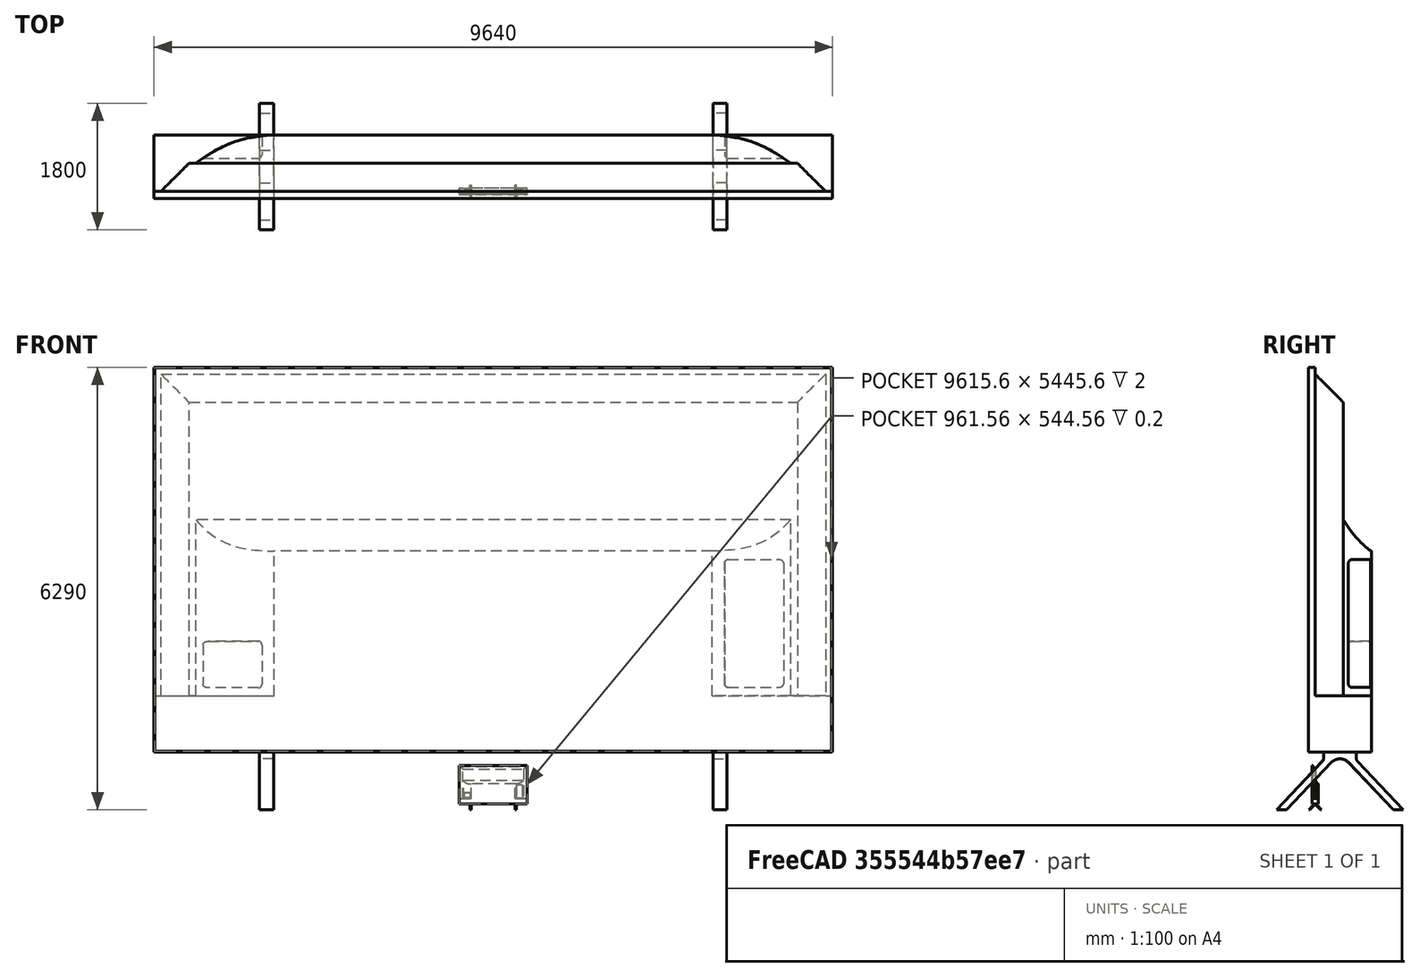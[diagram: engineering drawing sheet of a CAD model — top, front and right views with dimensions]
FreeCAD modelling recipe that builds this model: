
FCSTD DOCUMENT  (FreeCAD 1.0R39109 (Git))
Label: tv
License: All rights reserved
LicenseURL: https://en.wikipedia.org/wiki/All_rights_reserved
objects: Sketcher::SketchObject×9, PartDesign::Pad×6, PartDesign::Pocket×3, PartDesign::Body×3, App::Link×3, PartDesign::Fillet×2, Assembly::JointGroup×2, Assembly::AssemblyObject×2, Part::FeaturePython×2, PartDesign::ShapeBinder×2, PartDesign::Plane×2, App::Part×1
note: 60 computed .brp shape members not serialized (recipe doc carries the construction recipe); baked Part::Feature solids carry a one-line shape summary decoded from their .brp

FEATURE [Sketcher::SketchObject] Sketch003
  ArcFitTolerance = 1e-06
  AttachmentSupport = -> [XZ_Plane]
  FullyConstrained = true
  MakeInternals = false
  MapMode = 5
  Placement = pos=(0,0,0) rot=(1,0,0;1.5708rad)
  sketch-geometry (5):
    g0: LineSegment StartX=-4820 StartY=820 StartZ=0 EndX=4820 EndY=820 EndZ=0
    g1: LineSegment StartX=4820 StartY=820 StartZ=0 EndX=4820 EndY=6290 EndZ=0
    g2: LineSegment StartX=4820 StartY=6290 StartZ=0 EndX=-4820 EndY=6290 EndZ=0
    g3: LineSegment StartX=-4820 StartY=6290 StartZ=0 EndX=-4820 EndY=820 EndZ=0
    g4: GeomPoint [constr] X=0 Y=3555 Z=0
  constraints (13):
    c: Coincident(g0,g1)
    c: Coincident(g1,g2)
    c: Coincident(g2,g3)
    c: Coincident(g3,g0)
    c: Horizontal(g0)
    c: Horizontal(g2)
    c: Vertical(g1)
    c: Vertical(g3)
    c: Symmetric(g2,g0,g4)
    c: Distance(g1,g3) = 9640
    c: PointOnObject(g4,g-2)
    c: DistanceY(g1,g1) = 5470
    c: DistanceY(g0) = 820
FEATURE [PartDesign::Pad] Pad
  Direction = (0,-1,2e-16)
  Length = 100
  Length2 = 10
  Placement = pos=(0,0,0) rot=(1,0,0;1.5708rad)
  Profile = -> Sketch003
  ReferenceAxis = -> Sketch003 [N_Axis]
  Refine = true
  Suppressed = false
  Type = 0
FEATURE [Sketcher::SketchObject] Sketch004
  ArcFitTolerance = 1e-06
  AttachmentSupport = -> [Pad]
  ExternalGeometry = -> [Pad]
  FullyConstrained = true
  MakeInternals = false
  MapMode = 5
  Placement = pos=(0,7.894e-13,0) rot=(-1,0,0;1.5708rad)
  sketch-geometry (4):
    g0: LineSegment StartX=-4820 StartY=-820 StartZ=0 EndX=-4820 EndY=-1620 EndZ=0
    g1: LineSegment StartX=-4820 StartY=-1620 StartZ=0 EndX=4820 EndY=-1620 EndZ=0
    g2: LineSegment StartX=4820 StartY=-1620 StartZ=0 EndX=4820 EndY=-820 EndZ=0
    g3: LineSegment StartX=4820 StartY=-820 StartZ=0 EndX=-4820 EndY=-820 EndZ=0
  constraints (10):
    c: Coincident(g0,g1)
    c: Coincident(g1,g2)
    c: Coincident(g2,g3)
    c: Coincident(g3,g0)
    c: Vertical(g0)
    c: Vertical(g2)
    c: Horizontal(g1)
    c: DistanceY(g0,g0) = 800
    c: Coincident(g2,g-3)
    c: Coincident(g0,g-4)
FEATURE [PartDesign::Pad] Pad001
  BaseFeature = -> Pad
  Direction = (0,1,2e-16)
  Length = 800
  Length2 = 10
  Placement = pos=(0,0,0) rot=(1,0,0;1.5708rad)
  Profile = -> Sketch004
  ReferenceAxis = -> Sketch004 [N_Axis]
  Refine = true
  Suppressed = false
  Type = 0
FEATURE [Sketcher::SketchObject] Sketch005
  ArcFitTolerance = 1e-06
  AttachmentSupport = -> [Pad001]
  ExternalGeometry = -> [Pad001]
  FullyConstrained = false
  MakeInternals = false
  MapMode = 5
  Placement = pos=(0,7.894e-13,0) rot=(-1,0,0;1.5708rad)
  sketch-geometry (4):
    g0: LineSegment StartX=-4720 StartY=-6190 StartZ=0 EndX=4720 EndY=-6190 EndZ=0
    g1: LineSegment StartX=4720 StartY=-6190 StartZ=0 EndX=4720 EndY=-963.315 EndZ=0
    g2: LineSegment StartX=4720 StartY=-963.315 StartZ=0 EndX=-4720 EndY=-963.315 EndZ=0
    g3: LineSegment StartX=-4720 StartY=-963.315 StartZ=0 EndX=-4720 EndY=-6190 EndZ=0
  constraints (11):
    c: Coincident(g0,g1)
    c: Coincident(g1,g2)
    c: Coincident(g2,g3)
    c: Coincident(g3,g0)
    c: Horizontal(g0)
    c: Horizontal(g2)
    c: Vertical(g1)
    c: Vertical(g3)
    c: DistanceY(g-3,g0) = 100
    c: DistanceX(g-3,g0) = 100
    c: DistanceX(g0,g-4) = 100
FEATURE [PartDesign::Pad] Pad002
  BaseFeature = -> Pad001
  Direction = (0,1,2e-16)
  Length = 400
  Length2 = 10
  Placement = pos=(0,0,0) rot=(1,0,0;1.5708rad)
  Profile = -> Sketch005
  ReferenceAxis = -> Sketch005 [N_Axis]
  Refine = true
  Suppressed = false
  TaperAngle = -45
  Type = 0
FEATURE [Sketcher::SketchObject] Sketch008
  ArcFitTolerance = 1e-06
  AttachmentSupport = -> [Pad002]
  ExternalGeometry = -> [Pad002]
  FullyConstrained = false
  MakeInternals = false
  MapMode = 5
  Placement = pos=(0,0,1620) rot=(0,0,1;3.14159rad)
  sketch-geometry (18):
    g0: LineSegment StartX=0 StartY=-400 StartZ=0 EndX=-4226.42 EndY=-400 EndZ=0
    g1: Circle [constr] CenterX=-4226.42 CenterY=-400 CenterZ=0 NormalX=0 NormalY=0 NormalZ=1 AngleXU=0 Radius=1
    g2: Circle [constr] CenterX=-3745.48 CenterY=-741.541 CenterZ=0 NormalX=0 NormalY=0 NormalZ=1 AngleXU=0 Radius=1
    g3: Circle [constr] CenterX=-3483.42 CenterY=-773.588 CenterZ=0 NormalX=0 NormalY=0 NormalZ=1 AngleXU=0 Radius=1
    g4: BSplineCurve PolesCount=4 KnotsCount=2 Degree=3 IsPeriodic=0
    g5: GeomPoint [constr] X=-4226.42 Y=-400 Z=0
    g6: GeomPoint [constr] X=-3109.89 Y=-800 Z=0
    g7: Circle [constr] CenterX=-3109.89 CenterY=-800 CenterZ=0 NormalX=0 NormalY=0 NormalZ=1 AngleXU=0 Radius=1
    g8: LineSegment StartX=-3109.89 StartY=-800 StartZ=0 EndX=0 EndY=-800 EndZ=0
    g9: Circle [constr] CenterX=4226.42 CenterY=-400 CenterZ=0 NormalX=0 NormalY=0 NormalZ=1 AngleXU=0 Radius=1
    g10: Circle [constr] CenterX=3745.48 CenterY=-741.541 CenterZ=0 NormalX=0 NormalY=0 NormalZ=1 AngleXU=0 Radius=1
    g11: Circle [constr] CenterX=3483.42 CenterY=-773.588 CenterZ=0 NormalX=0 NormalY=0 NormalZ=1 AngleXU=0 Radius=1
    g12: BSplineCurve PolesCount=4 KnotsCount=2 Degree=3 IsPeriodic=0
    g13: GeomPoint [constr] X=4226.42 Y=-400 Z=0
    g14: GeomPoint [constr] X=3109.89 Y=-800 Z=0
    g15: Circle [constr] CenterX=3109.89 CenterY=-800 CenterZ=0 NormalX=0 NormalY=0 NormalZ=1 AngleXU=0 Radius=1
    g16: LineSegment StartX=3109.89 StartY=-800 StartZ=0 EndX=0 EndY=-800 EndZ=0
    g17: LineSegment StartX=0 StartY=-400 StartZ=0 EndX=4226.42 EndY=-400 EndZ=0
  constraints (25):
    c: Horizontal(g0)
    c: PointOnObject(g0,g-3)
    c: Weight(g1) = 1
    c: Equal(g1,g2)
    c: Equal(g1,g3)
    c: InternalAlignment(g1,g4)
    c: InternalAlignment(g2,g4)
    c: InternalAlignment(g3,g4)
    c: InternalAlignment(g5,g4)
    c: InternalAlignment(g6,g4)
    c: Coincident(g1,g0)
    c: InternalAlignment(g7,g4)
    c: Equal(g7,g1)
    c: Horizontal(g17)
    c: Weight(g9) = 1
    c: Equal(g9,g10)
    c: Equal(g9,g11)
    c: InternalAlignment(g9,g12)
    c: InternalAlignment(g10,g12)
    c: InternalAlignment(g11,g12)
    c: InternalAlignment(g13,g12)
    c: InternalAlignment(g14,g12)
    c: Coincident(g9,g17)
    c: InternalAlignment(g15,g12)
    c: Equal(g15,g9)
FEATURE [PartDesign::Pad] Pad003
  BaseFeature = -> Pad002
  Direction = (0,0,1)
  Length = 2500
  Length2 = 10
  Placement = pos=(0,0,0) rot=(1,0,0;1.5708rad)
  Profile = -> Sketch008
  ReferenceAxis = -> Sketch008 [N_Axis]
  Refine = true
  Suppressed = false
  Type = 0
FEATURE [Sketcher::SketchObject] Sketch009
  ArcFitTolerance = 1e-06
  AttachmentSupport = -> [Pad003]
  ExternalGeometry = -> [Pad003]
  FullyConstrained = false
  MakeInternals = false
  MapMode = 5
  Placement = pos=(4820,-4.5308e-12,0) rot=(0.707107,0,0.707107;3.14159rad)
  sketch-geometry (8):
    g0: LineSegment StartX=4120 StartY=-800 StartZ=0 EndX=3674.07 EndY=-800 EndZ=0
    g1: Circle [constr] CenterX=4120 CenterY=-400 CenterZ=0 NormalX=0 NormalY=0 NormalZ=1 AngleXU=0 Radius=1
    g2: Circle [constr] CenterX=3794.85 CenterY=-604.641 CenterZ=0 NormalX=0 NormalY=0 NormalZ=1 AngleXU=0 Radius=1
    g3: Circle [constr] CenterX=3674.07 CenterY=-800 CenterZ=0 NormalX=0 NormalY=0 NormalZ=1 AngleXU=0 Radius=1
    g4: BSplineCurve PolesCount=3 KnotsCount=2 Degree=2 IsPeriodic=0
    g5: GeomPoint [constr] X=4120 Y=-400 Z=0
    g6: GeomPoint [constr] X=3674.07 Y=-800 Z=0
    g7: LineSegment StartX=4120 StartY=-400 StartZ=0 EndX=4120 EndY=-800 EndZ=0
  constraints (12):
    c: Coincident(g0,g-4)
    c: Horizontal(g0)
    c: Weight(g1) = 1
    c: Equal(g1,g2)
    c: Equal(g1,g3)
    c: InternalAlignment(g1,g4)
    c: InternalAlignment(g2,g4)
    c: InternalAlignment(g3,g4)
    c: InternalAlignment(g5,g4)
    c: InternalAlignment(g6,g4)
    c: Coincident(g1,g-4)
    c: Coincident(g3,g0)
FEATURE [PartDesign::Pocket] Pocket
  BaseFeature = -> Pad003
  Direction = (-1,0,2e-16)
  Length = 5
  Length2 = 5
  Placement = pos=(0,0,0) rot=(1,0,0;1.5708rad)
  Profile = -> Sketch009
  ReferenceAxis = -> Sketch009 [N_Axis]
  Refine = true
  Suppressed = false
  Type = 1
FEATURE [Sketcher::SketchObject] Sketch010
  ArcFitTolerance = 1e-06
  AttachmentSupport = -> [Pocket]
  ExternalGeometry = -> [Pocket]
  FullyConstrained = false
  MakeInternals = false
  MapMode = 5
  Placement = pos=(0,800,0) rot=(-1,0,0;1.5708rad)
  sketch-geometry (13):
    g0: LineSegment StartX=4524.01 StartY=-3554.92 StartZ=0 EndX=4524.01 EndY=-1739.15 EndZ=0
    g1: LineSegment StartX=4524.01 StartY=-1739.15 StartZ=0 EndX=3287.44 EndY=-1739.15 EndZ=0
    g2: LineSegment StartX=3287.44 StartY=-1739.15 StartZ=0 EndX=3287.44 EndY=-3554.92 EndZ=0
    g3: LineSegment StartX=3287.44 StartY=-3554.92 StartZ=0 EndX=4524.01 EndY=-3554.92 EndZ=0
    g4: LineSegment StartX=-3287.44 StartY=-2395.51 StartZ=0 EndX=-3287.44 EndY=-1732.57 EndZ=0
    g5: LineSegment StartX=-3287.44 StartY=-1732.57 StartZ=0 EndX=-4524.01 EndY=-1732.57 EndZ=0
    g6: LineSegment StartX=-4524.01 StartY=-1732.57 StartZ=0 EndX=-4524.01 EndY=-2395.51 EndZ=0
    g7: LineSegment StartX=-4524.01 StartY=-2395.51 StartZ=0 EndX=-3287.44 EndY=-2395.51 EndZ=0
    g8: LineSegment [constr] StartX=3287.44 StartY=-3554.92 StartZ=0 EndX=3109.89 EndY=-3554.92 EndZ=0
    g9: LineSegment [constr] StartX=3109.89 StartY=-3554.92 StartZ=0 EndX=3109.89 EndY=-3674.07 EndZ=0
    g10: LineSegment [constr] StartX=3287.44 StartY=-1739.15 StartZ=0 EndX=3109.89 EndY=-1739.15 EndZ=0
    g11: LineSegment [constr] StartX=3109.89 StartY=-1739.15 StartZ=0 EndX=3109.89 EndY=-1620 EndZ=0
    g12: LineSegment [constr] StartX=-3287.44 StartY=-1732.57 StartZ=0 EndX=-3109.89 EndY=-1732.57 EndZ=0
  constraints (32):
    c: Coincident(g0,g1)
    c: Coincident(g1,g2)
    c: Coincident(g2,g3)
    c: Coincident(g3,g0)
    c: Vertical(g0)
    c: Vertical(g2)
    c: Horizontal(g1)
    c: Horizontal(g3)
    c: Coincident(g4,g5)
    c: Coincident(g5,g6)
    c: Coincident(g6,g7)
    c: Coincident(g7,g4)
    c: Vertical(g4)
    c: Vertical(g6)
    c: Horizontal(g5)
    c: Horizontal(g7)
    c: Coincident(g8,g2)
    c: PointOnObject(g8,g-3)
    c: Horizontal(g8)
    c: Coincident(g9,g8)
    c: Coincident(g9,g-3)
    c: Coincident(g10,g1)
    c: PointOnObject(g10,g-3)
    c: Horizontal(g10)
    c: Coincident(g11,g10)
    c: Coincident(g11,g-3)
    c: Equal(g9,g11)
    c: Coincident(g12,g4)
    c: PointOnObject(g12,g-4)
    c: Horizontal(g12)
    c: Equal(g12,g10)
    c: Equal(g3,g7)
FEATURE [PartDesign::Pocket] Pocket001
  BaseFeature = -> Pocket
  Direction = (0,-1,-2e-16)
  Length = 330
  Length2 = 5
  Placement = pos=(0,0,0) rot=(1,0,0;1.5708rad)
  Profile = -> Sketch010
  ReferenceAxis = -> Sketch010 [N_Axis]
  Refine = true
  Suppressed = false
  Type = 0
FEATURE [PartDesign::Fillet] Fillet
  Base = -> Pocket001 [Edge54,Edge57]
  BaseFeature = -> Pocket001
  Placement = pos=(0,0,0) rot=(1,0,0;1.5708rad)
  Radius = 50
  Refine = true
  SupportTransform = false
  Suppressed = false
  UseAllEdges = false
FEATURE [PartDesign::Fillet] Fillet001
  Base = -> Fillet [Edge16,Edge1,Edge62,Edge64]
  BaseFeature = -> Fillet
  Placement = pos=(0,0,0) rot=(1,0,0;1.5708rad)
  Radius = 50
  Refine = true
  SupportTransform = false
  Suppressed = false
  UseAllEdges = false
FEATURE [Sketcher::SketchObject] Sketch011
  ArcFitTolerance = 1e-06
  AttachmentSupport = -> [Fillet001]
  ExternalGeometry = -> [Fillet001]
  FullyConstrained = true
  MakeInternals = false
  MapMode = 5
  Placement = pos=(0,-100,0) rot=(1,0,0;1.5708rad)
  sketch-geometry (4):
    g0: LineSegment StartX=-4807.8 StartY=6277.8 StartZ=0 EndX=-4807.8 EndY=832.2 EndZ=0
    g1: LineSegment StartX=-4807.8 StartY=832.2 StartZ=0 EndX=4807.8 EndY=832.2 EndZ=0
    g2: LineSegment StartX=4807.8 StartY=832.2 StartZ=0 EndX=4807.8 EndY=6277.8 EndZ=0
    g3: LineSegment StartX=4807.8 StartY=6277.8 StartZ=0 EndX=-4807.8 EndY=6277.8 EndZ=0
  constraints (12):
    c: Coincident(g0,g1)
    c: Coincident(g1,g2)
    c: Coincident(g2,g3)
    c: Coincident(g3,g0)
    c: Vertical(g0)
    c: Vertical(g2)
    c: Horizontal(g1)
    c: Horizontal(g3)
    c: DistanceY(g0,g-3) = 12.2
    c: DistanceX(g-3,g0) = 12.2
    c: DistanceX(g1,g-4) = 12.2
    c: DistanceY(g-4,g1) = 12.2
FEATURE [PartDesign::Pocket] Pocket002
  BaseFeature = -> Fillet001
  Direction = (0,1,-2e-16)
  Length = 2
  Length2 = 5
  Placement = pos=(0,0,0) rot=(1,0,0;1.5708rad)
  Profile = -> Sketch011
  ReferenceAxis = -> Sketch011 [N_Axis]
  Refine = true
  Suppressed = false
  Type = 0
FEATURE [PartDesign::Body] Body
  AllowCompound = false
  Group = -> [Sketch003,Pad,Sketch004,Pad001,Sketch005,Pad002,Sketch008,Pad003,Sketch009,Pocket,Sketch010,Pocket001,Fillet,Fillet001,Sketch011,Pocket002]
  Origin = -> Origin
  Tip = -> Pocket002
FEATURE [Assembly::JointGroup] Joints
FEATURE [App::Link] Body003  label="Screen"
  LinkPlacement = pos=(0,-350,0) rot=(0,0,1;0rad)
  LinkedObject = -> Body
  Placement = pos=(0,-350,0) rot=(0,0,1;0rad)
FEATURE [Assembly::AssemblyObject] Assembly  label="Screen_a"
  Group = -> [Joints,Body003]
  Origin = -> Origin003
  Placement = pos=(0,-350,0) rot=(0,0,1;0rad)
  Type = Assembly
FEATURE [Part::FeaturePython] Clone001  label="Screen_clone"  # Draft clone (typed FeaturePython)
  AttacherType = Attacher::AttachEngine3D
  Fuse = false
  Objects = -> [Assembly]
  Scale = (0.1,0.1,0.1)
FEATURE [Assembly::JointGroup] Joints001
FEATURE [PartDesign::ShapeBinder] CopyFillet001
  Placement = pos=(0,0,0) rot=(1,0,0;1.5708rad)
  TraceSupport = false
FEATURE [PartDesign::Plane] DatumPlane
  AttachmentOffset = pos=(0,0,-1500) rot=(0,0,1;0rad)
  AttachmentSupport = -> [CopyFillet001]
  Length = 6989.3
  MapMode = 5
  Placement = pos=(3320,0,3.331e-13) rot=(0.707107,0,0.707107;3.14159rad)
  ResizeMode = 0
  Width = 2474.3
FEATURE [Sketcher::SketchObject] Sketch006
  ArcFitTolerance = 1e-06
  AttachmentSupport = -> [DatumPlane]
  ExternalGeometry = -> [CopyFillet001]
  FullyConstrained = false
  MakeInternals = false
  MapMode = 5
  Placement = pos=(3320,0,3.331e-13) rot=(0.707107,0,0.707107;3.14159rad)
  sketch-geometry (17):
    g0: LineSegment StartX=820 StartY=-119.068 StartZ=0 EndX=820 EndY=-580.932 EndZ=0
    g1: LineSegment StartX=820 StartY=-119.068 StartZ=0 EndX=736.366 EndY=-119.068 EndZ=0
    g2: LineSegment StartX=820 StartY=-580.932 StartZ=0 EndX=742.416 EndY=-580.932 EndZ=0
    g3: LineSegment StartX=680.048 StartY=-96.5682 StartZ=0 EndX=0 EndY=550 EndZ=0
    g4: LineSegment StartX=686.36 StartY=-603.183 StartZ=0 EndX=0 EndY=-1250 EndZ=0
    g5: LineSegment [constr] StartX=820 StartY=-350 StartZ=0 EndX=0 EndY=-350 EndZ=0
    g6: LineSegment [constr] StartX=820 StartY=100 StartZ=0 EndX=820 EndY=-119.068 EndZ=0
    g7: LineSegment [constr] StartX=820 StartY=-580.932 StartZ=0 EndX=820 EndY=-800 EndZ=0
    g8: LineSegment StartX=0 StartY=408.983 StartZ=0 EndX=671.046 EndY=-229.026 EndZ=0
    g9: LineSegment StartX=670.497 StartY=-477.115 StartZ=0 EndX=0 EndY=-1108.98 EndZ=0
    g10: ArcOfCircle CenterX=553.355 CenterY=-352.811 CenterZ=0 NormalX=0 NormalY=0 NormalZ=1 AngleXU=0 Radius=170.803 StartAngle=5.46813 EndAngle=7.09382
    g11: LineSegment StartX=0 StartY=550 StartZ=0 EndX=0 EndY=408.983 EndZ=0
    g12: LineSegment StartX=0 StartY=-1108.98 StartZ=0 EndX=0 EndY=-1250 EndZ=0
    g13: ArcOfCircle CenterX=736.366 CenterY=-37.3338 CenterZ=0 NormalX=0 NormalY=0 NormalZ=1 AngleXU=0 Radius=81.7339 StartAngle=3.95222 EndAngle=4.71239
    g14: GeomPoint [constr] X=703.713 Y=-119.068 Z=0
    g15: ArcOfCircle CenterX=742.416 CenterY=-662.666 CenterZ=0 NormalX=0 NormalY=0 NormalZ=1 AngleXU=0 Radius=81.7339 StartAngle=1.5708 EndAngle=2.32654
    g16: GeomPoint [constr] X=709.972 Y=-580.932 Z=0
  constraints (37):
    c: PointOnObject(g0,g-3)
    c: PointOnObject(g0,g-3)
    c: Coincident(g1,g0)
    c: Horizontal(g1)
    c: Coincident(g2,g0)
    c: Horizontal(g2)
    c: PointOnObject(g3,g-2)
    c: DistanceY(g4,g3) = 1800
    c: PointOnObject(g4,g-2)
    c: Symmetric(g0,g0,g5)
    c: Horizontal(g5)
    c: Symmetric(g4,g3,g5)
    c: Coincident(g6,g-3)
    c: Coincident(g6,g0)
    c: Coincident(g7,g0)
    c: Coincident(g7,g-3)
    c: Equal(g7,g6)
    c: PointOnObject(g8,g-2)
    c: PointOnObject(g9,g-2)
    c: Parallel(g8,g3)
    c: Parallel(g9,g4)
    c: Tangent(g8,g10) = 1.5708
    c: Tangent(g9,g10) = 1.5708
    c: Coincident(g11,g3)
    c: Coincident(g11,g8)
    c: Coincident(g12,g9)
    c: Coincident(g12,g4)
    c: PointOnObject(g14,g1)
    c: PointOnObject(g14,g3)
    c: Tangent(g1,g13) = 1.5708
    c: Tangent(g3,g13) = 1.5708
    c: PointOnObject(g16,g2)
    c: PointOnObject(g16,g4)
    c: Tangent(g2,g15) = -1.5708
    c: Tangent(g4,g15) = -1.5708
    c: Equal(g13,g15)
    c: Equal(g12,g11)
FEATURE [PartDesign::Pad] Pad004
  Direction = (1,0,-2e-16)
  Length = 200
  Length2 = 10
  Placement = pos=(3320,0,3.331e-13) rot=(0.707107,0,0.707107;3.14159rad)
  Profile = -> Sketch006
  ReferenceAxis = -> Sketch006 [N_Axis]
  Refine = true
  Reversed = true
  Suppressed = false
  Type = 0
FEATURE [PartDesign::Body] Body001
  AllowCompound = false
  Group = -> [DatumPlane,CopyFillet001,Sketch006,Pad004]
  Origin = -> Origin001
  Tip = -> Pad004
FEATURE [App::Link] Body004  label="Right_Stand"
  LinkPlacement = pos=(0,-350,0) rot=(0,0,1;0rad)
  LinkedObject = -> Body001
  Placement = pos=(0,-350,0) rot=(0,0,1;0rad)
FEATURE [PartDesign::ShapeBinder] CopyFillet002
  Placement = pos=(0,0,0) rot=(1,0,0;1.5708rad)
  TraceSupport = false
FEATURE [PartDesign::Plane] DatumPlane001
  AttachmentOffset = pos=(0,0,-1500) rot=(0,0,1;0rad)
  AttachmentSupport = -> [CopyFillet002]
  Length = 6989.3
  MapMode = 5
  Placement = pos=(-3320,0,3.331e-13) rot=(0.707107,0,-0.707107;3.14159rad)
  ResizeMode = 0
  Width = 2474.3
FEATURE [Sketcher::SketchObject] Sketch007
  ArcFitTolerance = 1e-06
  AttachmentSupport = -> [DatumPlane001]
  FullyConstrained = false
  MakeInternals = false
  MapMode = 5
  Placement = pos=(-3320,0,3.331e-13) rot=(0.707107,0,-0.707107;3.14159rad)
  sketch-geometry (17):
    g0: LineSegment StartX=-820 StartY=-580.932 StartZ=0 EndX=-820 EndY=-119.068 EndZ=0
    g1: LineSegment StartX=-820 StartY=-580.932 StartZ=0 EndX=-736.366 EndY=-580.932 EndZ=0
    g2: LineSegment StartX=-820 StartY=-119.068 StartZ=0 EndX=-742.416 EndY=-119.068 EndZ=0
    g3: LineSegment StartX=-680.048 StartY=-603.432 StartZ=0 EndX=0 EndY=-1250 EndZ=0
    g4: LineSegment StartX=-686.36 StartY=-96.8166 StartZ=0 EndX=0 EndY=550 EndZ=0
    g5: LineSegment [constr] StartX=-820 StartY=-350 StartZ=0 EndX=0 EndY=-350 EndZ=0
    g6: LineSegment [constr] StartX=-820 StartY=-800 StartZ=0 EndX=-820 EndY=-580.932 EndZ=0
    g7: LineSegment [constr] StartX=-820 StartY=-119.068 StartZ=0 EndX=-820 EndY=100 EndZ=0
    g8: LineSegment StartX=0 StartY=-1108.98 StartZ=0 EndX=-671.046 EndY=-470.974 EndZ=0
    g9: LineSegment StartX=-670.497 StartY=-222.885 StartZ=0 EndX=0 EndY=408.983 EndZ=0
    g10: ArcOfCircle CenterX=-553.355 CenterY=-347.189 CenterZ=0 NormalX=0 NormalY=0 NormalZ=1 AngleXU=0 Radius=170.803 StartAngle=2.32654 EndAngle=3.95222
    g11: LineSegment StartX=0 StartY=-1250 StartZ=0 EndX=0 EndY=-1108.98 EndZ=0
    g12: LineSegment StartX=0 StartY=408.983 StartZ=0 EndX=0 EndY=550 EndZ=0
    g13: ArcOfCircle CenterX=-736.366 CenterY=-662.666 CenterZ=0 NormalX=0 NormalY=0 NormalZ=1 AngleXU=0 Radius=81.734 StartAngle=0.81063 EndAngle=1.5708
    g14: GeomPoint [constr] X=-703.713 Y=-580.932 Z=0
    g15: ArcOfCircle CenterX=-742.416 CenterY=-37.3338 CenterZ=0 NormalX=0 NormalY=0 NormalZ=1 AngleXU=0 Radius=81.734 StartAngle=4.71239 EndAngle=5.46813
    g16: GeomPoint [constr] X=-709.972 Y=-119.068 Z=0
  constraints (25):
    c: Coincident(g1,g0)
    c: Coincident(g2,g0)
    c: Symmetric(g0,g0,g5)
    c: Symmetric(g4,g3,g5)
    c: Coincident(g6,g0)
    c: Coincident(g7,g0)
    c: Equal(g7,g6)
    c: Parallel(g8,g3)
    c: Parallel(g9,g4)
    c: Tangent(g8,g10) = 1.5708
    c: Tangent(g9,g10) = 1.5708
    c: Coincident(g11,g3)
    c: Coincident(g11,g8)
    c: Coincident(g12,g9)
    c: Coincident(g12,g4)
    c: PointOnObject(g14,g1)
    c: PointOnObject(g14,g3)
    c: Tangent(g1,g13) = 1.5708
    c: Tangent(g3,g13) = 1.5708
    c: PointOnObject(g16,g2)
    c: PointOnObject(g16,g4)
    c: Tangent(g2,g15) = -1.5708
    c: Tangent(g4,g15) = -1.5708
    c: Equal(g13,g15)
    c: Equal(g12,g11)
FEATURE [PartDesign::Pad] Pad005
  Direction = (-1,0,-2e-16)
  Length = 200
  Length2 = 10
  Placement = pos=(-3320,0,3.331e-13) rot=(0.707107,0,-0.707107;3.14159rad)
  Profile = -> Sketch007
  ReferenceAxis = -> Sketch007 [N_Axis]
  Refine = true
  Reversed = true
  Suppressed = false
  Type = 0
FEATURE [PartDesign::Body] Body002
  AllowCompound = false
  Group = -> [DatumPlane001,CopyFillet002,Sketch007,Pad005]
  Origin = -> Origin002
  Tip = -> Pad005
FEATURE [App::Link] Body005  label="Left_Stand"
  LinkPlacement = pos=(0,-350,0) rot=(0,0,1;0rad)
  LinkedObject = -> Body002
  Placement = pos=(0,-350,0) rot=(0,0,1;0rad)
FEATURE [Assembly::AssemblyObject] Assembly001  label="Stand_a"
  Group = -> [Joints001,Body004,Body005]
  Origin = -> Origin005
  Placement = pos=(0,-350,0) rot=(0,0,1;0rad)
  Type = Assembly
FEATURE [Part::FeaturePython] Clone  label="Stand_clone"  # Draft clone (typed FeaturePython)
  AttacherType = Attacher::AttachEngine3D
  Fuse = false
  Objects = -> [Assembly001]
  Scale = (0.1,0.1,0.1)
FEATURE [App::Part] Part001  label="tv"
  Group = -> [Clone001,Clone]
  Origin = -> Origin004
